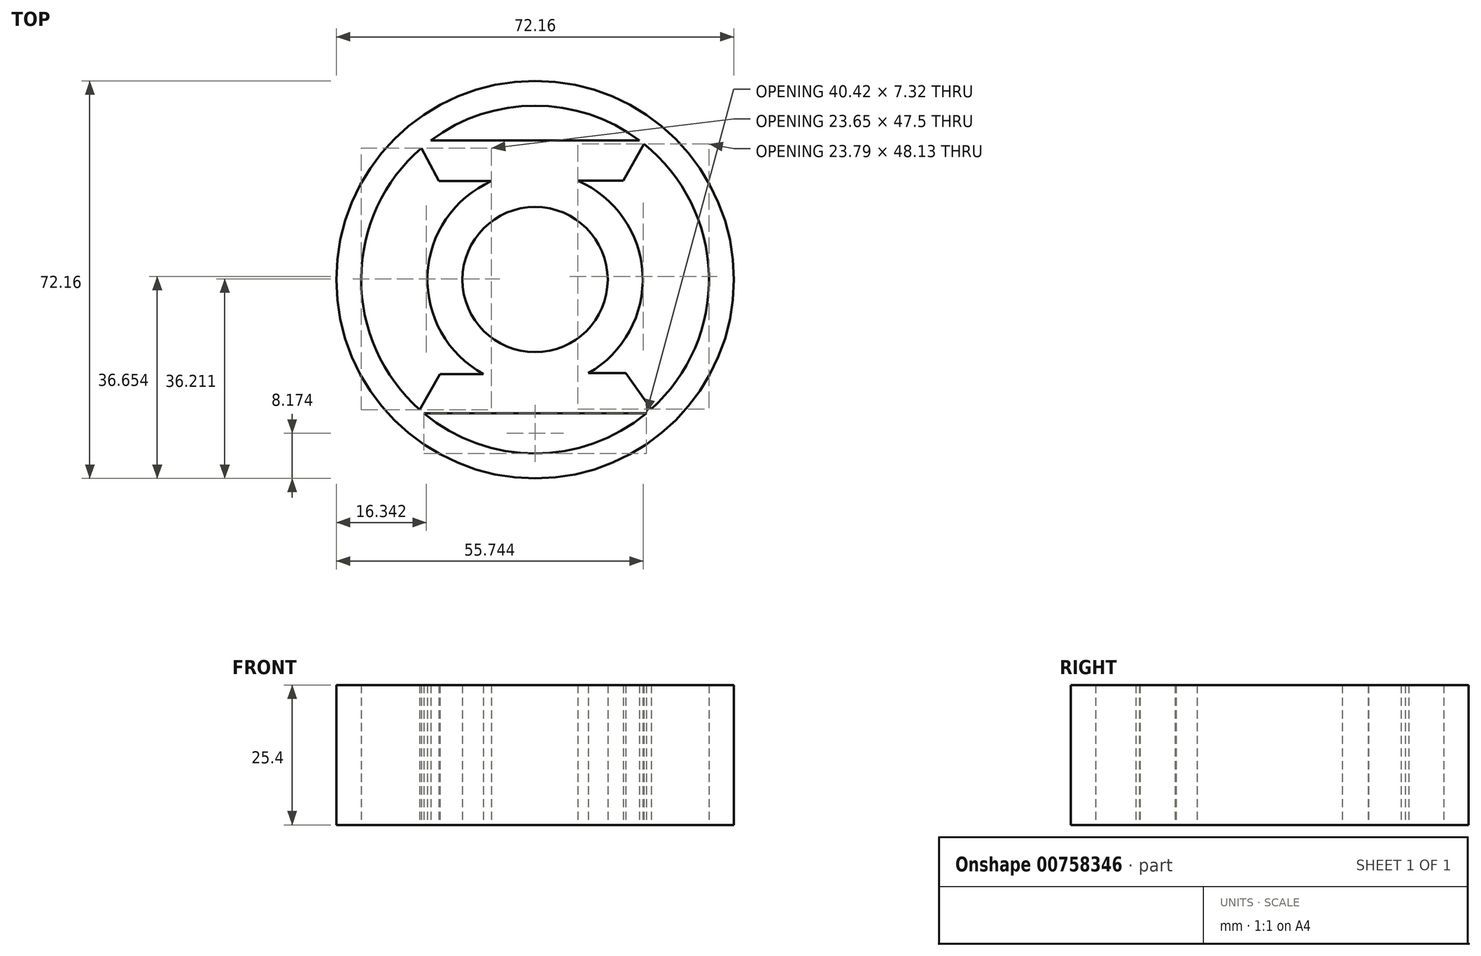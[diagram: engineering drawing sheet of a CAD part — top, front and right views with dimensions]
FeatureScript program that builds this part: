
annotation { "Feature Type Name" : "Feature", "Feature Type Description" : "" }
export const myFeature = defineFeature(function(context is Context, id is Id, definition is map)
    precondition{}
    {
        {
            var Q0;
            Q0=qCreatedBy(makeId("Top.planeOp"),FACE);
            var sketch = newSketch(context, id + "F0", { "sketchPlane" : qUnion([Q0])});
            skCircle(sketch, "E0", {"center": v(39.6, 43.05) * mm, "radius": 36.08 * mm});
            skArc(sketch, "E1", {"start": v(60.68, 19.56) * mm, "mid": v(71.15, 43.94) * mm, "end": v(59.33, 67.69) * mm});
            skArc(sketch, "E2", {"start": v(49.26, 26.07) * mm, "mid": v(59.1, 44.11) * mm, "end": v(47.36, 60.98) * mm});
            skCircle(sketch, "E3", {"center": v(39.6, 43.05) * mm, "radius": 13.19 * mm});
            skLineSegment(sketch, "E4", {"start": v(58.5, 68.32) * mm, "end": v(20.68, 68.32) * mm});
            skLineSegment(sketch, "E5", {"start": v(18.95, 66.93) * mm, "end": v(22.14, 60.92) * mm});
            skLineSegment(sketch, "E6", {"start": v(22.14, 60.92) * mm, "end": v(31.68, 60.92) * mm});
            skLineSegment(sketch, "E7", {"start": v(55.62, 60.98) * mm, "end": v(59.33, 67.69) * mm});
            skLineSegment(sketch, "E8", {"start": v(55.62, 60.98) * mm, "end": v(47.36, 60.98) * mm});
            skLineSegment(sketch, "E9", {"start": v(59.8, 18.8) * mm, "end": v(19.38, 18.8) * mm});
            skLineSegment(sketch, "E10", {"start": v(18.65, 19.43) * mm, "end": v(22.3, 25.9) * mm});
            skLineSegment(sketch, "E11", {"start": v(22.3, 25.9) * mm, "end": v(30.23, 25.9) * mm});
            skLineSegment(sketch, "E12", {"start": v(60.68, 19.56) * mm, "end": v(56.07, 26.07) * mm});
            skLineSegment(sketch, "E13", {"start": v(56.07, 26.07) * mm, "end": v(49.26, 26.07) * mm});
            skArc(sketch, "E14.trimOffspring", {"start": v(19.38, 18.8) * mm, "mid": v(39.6, 11.48) * mm, "end": v(59.8, 18.8) * mm});
            skArc(sketch, "E15.trimOffspring", {"start": v(18.95, 66.93) * mm, "mid": v(8.03, 43.25) * mm, "end": v(18.65, 19.43) * mm});
            skArc(sketch, "E16.trimOffspring", {"start": v(31.68, 60.92) * mm, "mid": v(20.07, 43.86) * mm, "end": v(30.23, 25.9) * mm});
            skArc(sketch, "E17.trimOffspring", {"start": v(58.5, 68.32) * mm, "mid": v(39.6, 74.62) * mm, "end": v(20.68, 68.32) * mm});
            skSolve(sketch);
        }
        {
            var Q0;
            Q0=makeQuery(id+"F0.imprint","IMPRINT",FACE,{"disambiguationData":[TD([[makeQuery(id+"F0.imprint","IMPRINT",EDGE,{"derivedFrom":sQuery(id+"F0.wireOp",EDGE,"E0")}),1.0]])]});
            extrude(context, id + "F1", {"entities" : qUnion([Q0]), "depth" : 25.4 * mm, "offsetDistance" : 25.4 * mm});
        }
    });
